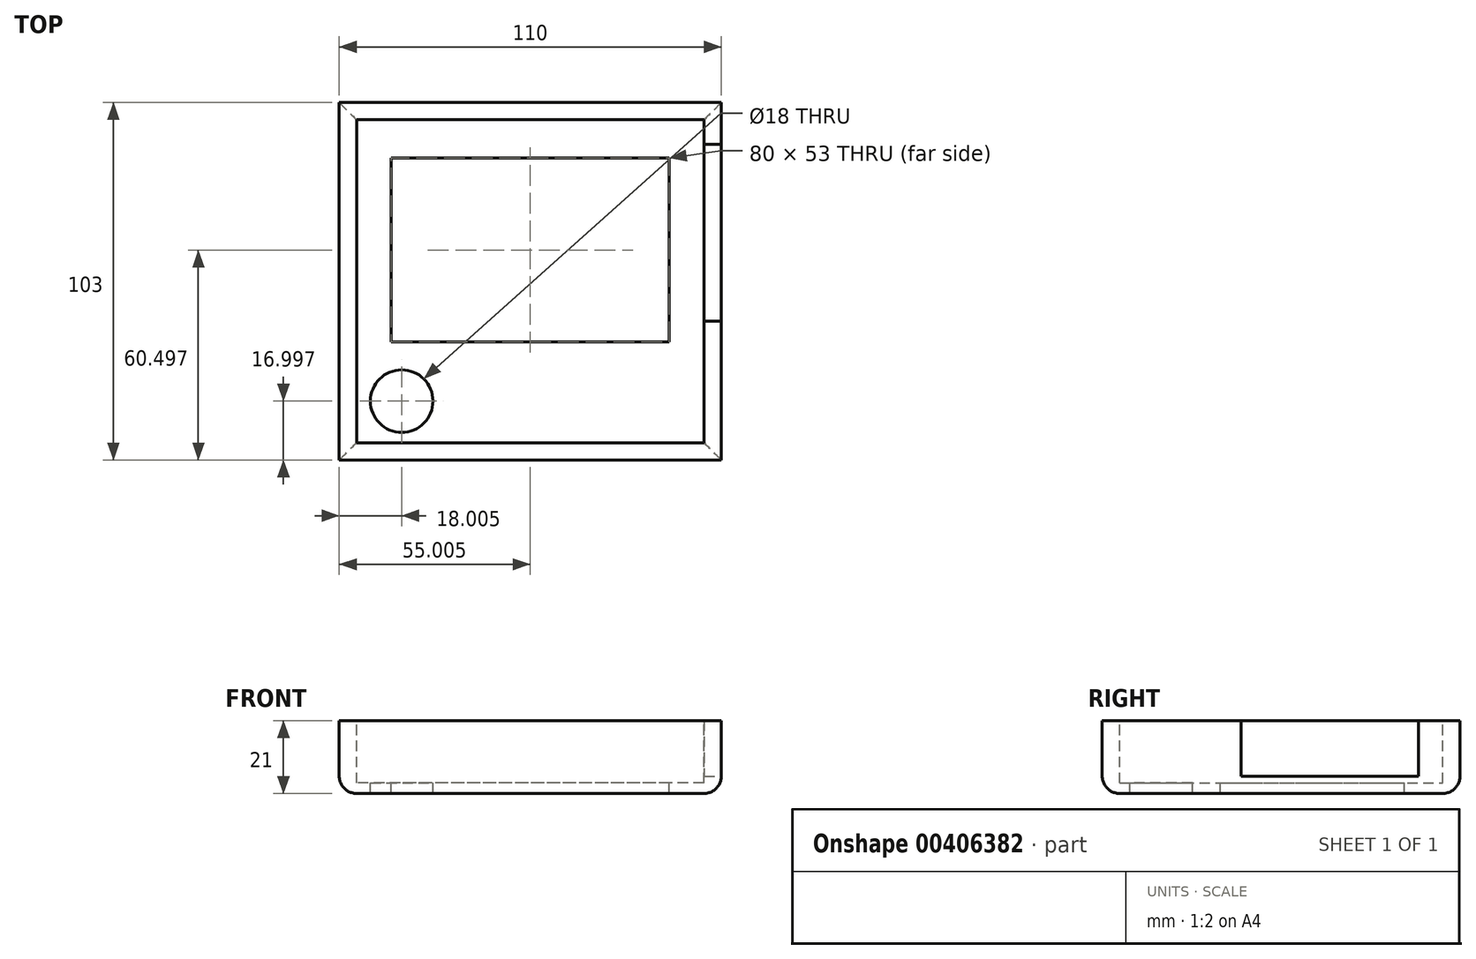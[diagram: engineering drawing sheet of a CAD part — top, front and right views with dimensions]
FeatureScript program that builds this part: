
annotation { "Feature Type Name" : "Feature", "Feature Type Description" : "" }
export const myFeature = defineFeature(function(context is Context, id is Id, definition is map)
    precondition{}
    {
        {
            var Q0;
            Q0=qCreatedBy(makeId("Top.planeOp"),FACE);
            var sketch = newSketch(context, id + "F0", { "sketchPlane" : qUnion([Q0])});
            skLineSegment(sketch, "E0.bottom", {"start": v(-63.3, -47.8) * mm, "end": v(46.7, -47.8) * mm});
            skLineSegment(sketch, "E0.top", {"start": v(-63.3, 55.2) * mm, "end": v(46.7, 55.2) * mm});
            skLineSegment(sketch, "E0.left", {"start": v(-63.3, -47.8) * mm, "end": v(-63.3, 55.2) * mm});
            skLineSegment(sketch, "E0.right", {"start": v(46.7, -47.8) * mm, "end": v(46.7, 55.2) * mm});
            skLineSegment(sketch, "E1.0", {"start": v(-48.3, 39.2) * mm, "end": v(31.7, 39.2) * mm});
            skLineSegment(sketch, "E2.0", {"start": v(-48.3, -13.8) * mm, "end": v(-48.3, 39.2) * mm});
            skLineSegment(sketch, "E3.0", {"start": v(31.7, -13.8) * mm, "end": v(31.7, 39.2) * mm});
            skLineSegment(sketch, "E4.0", {"start": v(-48.3, -13.8) * mm, "end": v(31.7, -13.8) * mm});
            skCircle(sketch, "E5", {"center": v(28.7, -30.8) * mm, "radius": 9 * mm});
            skSolve(sketch);
        }
        {
            var Q0;
            Q0=makeQuery(id+"F0.imprint","IMPRINT",FACE,{"disambiguationData":[TD([[makeQuery(id+"F0.imprint","IMPRINT",EDGE,{"derivedFrom":sQuery(id+"F0.wireOp",EDGE,"E0.bottom")}),1.0]])]});
            extrude(context, id + "F1", {"entities" : qUnion([Q0]), "depth" : 21 * mm});
        }
        {
            var Q0;
            Q0=makeQuery(id+"F1.opExtrude","CAP_FACE",FACE,{"disambiguationData":[OSD([sQuery(id+"F0.wireOp",EDGE,"E0.bottom"),sQuery(id+"F0.wireOp",EDGE,"E0.top"),sQuery(id+"F0.wireOp",EDGE,"E0.left"),sQuery(id+"F0.wireOp",EDGE,"E0.right"),sQuery(id+"F0.wireOp",EDGE,"E1.0"),sQuery(id+"F0.wireOp",EDGE,"E2.0"),sQuery(id+"F0.wireOp",EDGE,"E3.0"),sQuery(id+"F0.wireOp",EDGE,"E4.0"),sQuery(id+"F0.wireOp",EDGE,"E5")])],"isStart":true});
            var sketch = newSketch(context, id + "F2", { "sketchPlane" : qUnion([Q0])});
            skLineSegment(sketch, "E6.bottom", {"start": v(-58.3, 42.8) * mm, "end": v(41.7, 42.8) * mm});
            skLineSegment(sketch, "E6.top", {"start": v(-58.3, -50.2) * mm, "end": v(41.7, -50.2) * mm});
            skLineSegment(sketch, "E6.left", {"start": v(-58.3, 42.8) * mm, "end": v(-58.3, -50.2) * mm});
            skLineSegment(sketch, "E6.right", {"start": v(41.7, 42.8) * mm, "end": v(41.7, -50.2) * mm});
            skSolve(sketch);
        }
        {
            var Q0;
            Q0=makeQuery(id+"F2.imprint","IMPRINT",FACE,{"disambiguationData":[TD([[makeQuery(id+"F2.imprint","IMPRINT",EDGE,{"derivedFrom":sQuery(id+"F2.wireOp",EDGE,"E6.bottom")}),-1.0]])]});
            extrude(context, id + "F3", {"entities" : qUnion([Q0]), "operationType" : NewBodyOperationType.REMOVE, "oppositeDirection" : true, "depth" : 18 * mm});
        }
        {
            var Q0;
            Q0=makeQuery(id+"F1.opExtrude","CAP_EDGE",EDGE,{"disambiguationData":[OSD([sQuery(id+"F0.wireOp",EDGE,"E0.bottom")])],"isStart":false});
            var Q1;
            Q1=makeQuery(id+"F1.opExtrude","CAP_EDGE",EDGE,{"disambiguationData":[OSD([sQuery(id+"F0.wireOp",EDGE,"E0.right")])],"isStart":false});
            var Q2;
            Q2=makeQuery(id+"F1.opExtrude","CAP_EDGE",EDGE,{"disambiguationData":[OSD([sQuery(id+"F0.wireOp",EDGE,"E0.top")])],"isStart":false});
            var Q3;
            Q3=makeQuery(id+"F1.opExtrude","CAP_EDGE",EDGE,{"disambiguationData":[OSD([sQuery(id+"F0.wireOp",EDGE,"E0.left")])],"isStart":false});
            fillet(context, id + "F4", {"entities" : qUnion([Q0, Q1, Q2, Q3]), "radius" : 5 * mm, "tangentPropagation" : true, "allowEdgeOverflow" : false});
        }
        {
            var Q0;
            Q0=makeQuery(id+"F1.opExtrude","SWEPT_BODY",BODY,{"disambiguationData":[OSD([sQuery(id+"F0.wireOp",EDGE,"E0.bottom"),sQuery(id+"F0.wireOp",EDGE,"E0.top"),sQuery(id+"F0.wireOp",EDGE,"E0.left"),sQuery(id+"F0.wireOp",EDGE,"E0.right"),sQuery(id+"F0.wireOp",EDGE,"E1.0"),sQuery(id+"F0.wireOp",EDGE,"E2.0"),sQuery(id+"F0.wireOp",EDGE,"E3.0"),sQuery(id+"F0.wireOp",EDGE,"E4.0"),sQuery(id+"F0.wireOp",EDGE,"E5")])]});
            var Q1;
            Q1=makeQuery(id+"F1.opExtrude","CAP_EDGE",EDGE,{"disambiguationData":[OSD([sQuery(id+"F0.wireOp",EDGE,"E0.right")])],"isStart":true});
            transform(context, id + "F5", {"entities" : qUnion([Q0]), "transformType" : TransformType.ROTATION, "transformAxis" : qUnion([Q1]), "angle" : 180 * degree, "makeCopy" : false});
        }
        {
            var Q0;
            Q0=makeQuery(id+"F1.opExtrude","SWEPT_BODY",BODY,{"disambiguationData":[OSD([sQuery(id+"F0.wireOp",EDGE,"E0.bottom"),sQuery(id+"F0.wireOp",EDGE,"E0.top"),sQuery(id+"F0.wireOp",EDGE,"E0.left"),sQuery(id+"F0.wireOp",EDGE,"E0.right"),sQuery(id+"F0.wireOp",EDGE,"E1.0"),sQuery(id+"F0.wireOp",EDGE,"E2.0"),sQuery(id+"F0.wireOp",EDGE,"E3.0"),sQuery(id+"F0.wireOp",EDGE,"E4.0"),sQuery(id+"F0.wireOp",EDGE,"E5")])]});
            transform(context, id + "F6", {"entities" : qUnion([Q0]), "transformType" : TransformType.TRANSLATION_3D, "dx" : -101.8 * mm, "dy" : -3.3 * mm, "dz" : 22.4 * mm, "makeCopy" : false});
        }
        {
            var Q0;
            Q0=makeQuery(id+"F1.opExtrude","SWEPT_FACE",FACE,{"disambiguationData":[OSD([sQuery(id+"F0.wireOp",EDGE,"E0.left")])]});
            var sketch = newSketch(context, id + "F7", { "sketchPlane" : qUnion([Q0])});
            skLineSegment(sketch, "E7.bottom", {"start": v(-11.1, 6.4) * mm, "end": v(39.9, 6.4) * mm});
            skLineSegment(sketch, "E7.top", {"start": v(-11.1, 22.4) * mm, "end": v(39.9, 22.4) * mm});
            skLineSegment(sketch, "E7.left", {"start": v(-11.1, 6.4) * mm, "end": v(-11.1, 22.4) * mm});
            skLineSegment(sketch, "E7.right", {"start": v(39.9, 6.4) * mm, "end": v(39.9, 22.4) * mm});
            skSolve(sketch);
        }
        {
            var Q0;
            Q0=makeQuery(id+"F7.imprint","IMPRINT",FACE,{"disambiguationData":[TD([[makeQuery(id+"F7.imprint","IMPRINT",EDGE,{"derivedFrom":sQuery(id+"F7.wireOp",EDGE,"E7.bottom")}),1.0]])]});
            var Q1;
            Q1=makeQuery(id+"F3.boolean.opBoolean","COPY",FACE,{"derivedFrom":makeQuery(id+"F3.opExtrude","SWEPT_FACE",FACE,{"disambiguationData":[OSD([sQuery(id+"F2.wireOp",EDGE,"E6.left")])]})});
            extrude(context, id + "F8", {"entities" : qUnion([Q0, Q1]), "operationType" : NewBodyOperationType.REMOVE, "oppositeDirection" : true, "depth" : 25 * mm});
        }
    });
